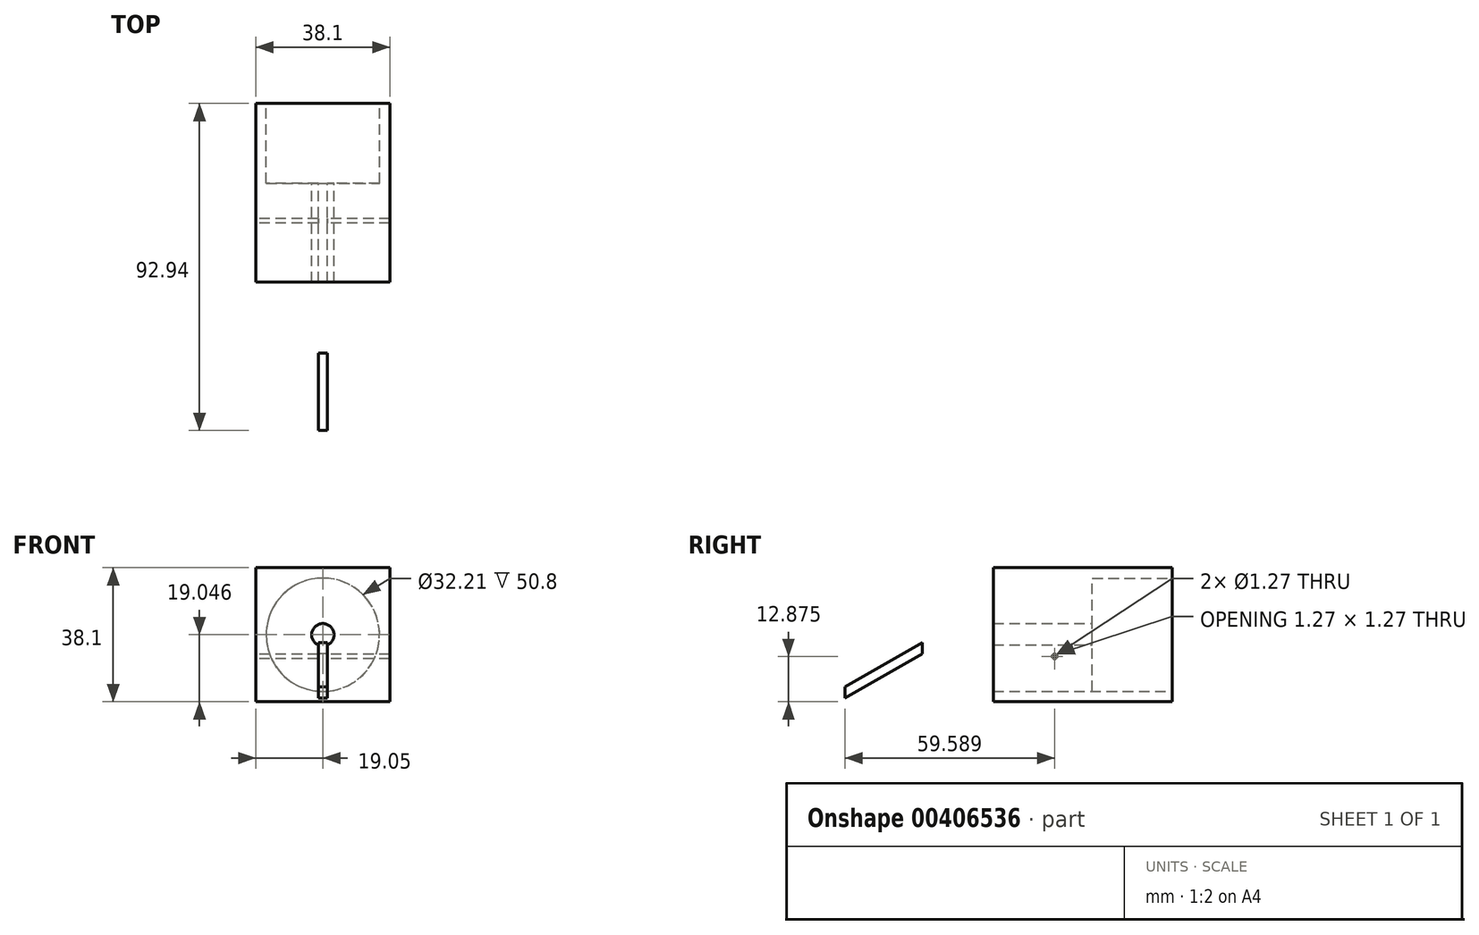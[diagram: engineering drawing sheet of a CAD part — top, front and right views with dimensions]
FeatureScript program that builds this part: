
annotation { "Feature Type Name" : "Feature", "Feature Type Description" : "" }
export const myFeature = defineFeature(function(context is Context, id is Id, definition is map)
    precondition{}
    {
        {
            var Q0;
            Q0=qCreatedBy(makeId("Right.planeOp"),FACE);
            var sketch = newSketch(context, id + "F0", { "sketchPlane" : qUnion([Q0])});
            skLineSegment(sketch, "E0.bottom", {"start": v(-13.06, 8.82) * mm, "end": v(37.74, 8.82) * mm});
            skLineSegment(sketch, "E0.top", {"start": v(-13.06, -29.28) * mm, "end": v(37.74, -29.28) * mm});
            skLineSegment(sketch, "E0.left", {"start": v(-13.06, 8.82) * mm, "end": v(-13.06, -29.28) * mm});
            skLineSegment(sketch, "E0.right", {"start": v(37.74, 8.82) * mm, "end": v(37.74, -29.28) * mm});
            skPoint(sketch, "E1", {"position": v(12.34, -10.23) * mm});
            skPoint(sketch, "E1.positionSnap0", {"position": v(12.34, 8.82) * mm});
            skPoint(sketch, "E1.positionSnap1", {"position": v(37.74, -10.23) * mm});
            skPoint(sketch, "E2", {"position": v(4.28, -10.23) * mm});
            skPoint(sketch, "E3", {"position": v(-3.68, -16.4) * mm});
            skPoint(sketch, "E4", {"position": v(4.28, -13.4) * mm});
            skPoint(sketch, "E5", {"position": v(4.28, -7.06) * mm});
            skLineSegment(sketch, "E6", {"start": v(4.28, -10.23) * mm, "end": v(4.28, -13.4) * mm});
            skPoint(sketch, "E7", {"position": v(-41.1, -18.58) * mm});
            skLineSegment(sketch, "E8", {"start": v(-33.14, -12.41) * mm, "end": v(-33.14, -15.59) * mm});
            skLineSegment(sketch, "E9", {"start": v(-33.14, -15.59) * mm, "end": v(-55.2, -28.18) * mm});
            skLineSegment(sketch, "E10", {"start": v(-33.14, -12.41) * mm, "end": v(-55.15, -25.09) * mm});
            skLineSegment(sketch, "E11", {"start": v(-55.15, -25.09) * mm, "end": v(-55.2, -28.18) * mm});
            skPoint(sketch, "E12", {"position": v(14.98, -10.23) * mm});
            skPoint(sketch, "E13", {"position": v(-33.14, -18.58) * mm});
            skPoint(sketch, "E14", {"position": v(12.34, -16.4) * mm});
            skPoint(sketch, "E15", {"position": v(4.39, -16.4) * mm});
            skCircle(sketch, "E16", {"center": v(4.39, -16.4) * mm, "radius": 0.64 * mm});
            skSolve(sketch);
        }
        {
            var Q0;
            Q0=makeQuery(id+"F0.imprint","IMPRINT",FACE,{"disambiguationData":[TD([[makeQuery(id+"F0.imprint","IMPRINT",EDGE,{"derivedFrom":sQuery(id+"F0.wireOp",EDGE,"E0.bottom")}),-1.0]])]});
            extrude(context, id + "F1", {"entities" : qUnion([Q0]), "endBound" : BoundingType.SYMMETRIC, "depth" : 38.1 * mm, "offsetDistance" : 25.4 * mm});
        }
        {
            var Q0;
            Q0=makeQuery(id+"F1.opExtrude","SWEPT_FACE",FACE,{"disambiguationData":[OSD([sQuery(id+"F0.wireOp",EDGE,"E0.right")])]});
            var sketch = newSketch(context, id + "F2", { "sketchPlane" : qUnion([Q0])});
            skPoint(sketch, "E17", {"position": v(0, -10.23) * mm});
            skPoint(sketch, "E17.positionSnap0", {"position": v(19.05, -10.23) * mm});
            skPoint(sketch, "E17.positionSnap1", {"position": v(0, -29.28) * mm});
            skCircle(sketch, "E18", {"center": v(0, -10.23) * mm, "radius": 16.1 * mm});
            skCircle(sketch, "E19", {"center": v(0, -10.23) * mm, "radius": 3.18 * mm});
            skPoint(sketch, "E20", {"position": v(-1.27, -29.28) * mm});
            skPoint(sketch, "E21.MirrorP", {"position": v(1.27, -29.28) * mm});
            skLineSegment(sketch, "E22", {"start": v(-1.27, -29.28) * mm, "end": v(-1.27, -13.14) * mm});
            skLineSegment(sketch, "E23", {"start": v(1.27, -29.28) * mm, "end": v(1.27, -13.14) * mm});
            skSolve(sketch);
        }
        {
            var Q0;
            Q0=makeQuery(id+"F2.imprint","IMPRINT",FACE,{"disambiguationData":[TD([[makeQuery(id+"F2.imprint","IMPRINT",EDGE,{"derivedFrom":sQuery(id+"F2.wireOp",EDGE,"E18")}),1.0]])]});
            extrude(context, id + "F3", {"entities" : qUnion([Q0]), "operationType" : NewBodyOperationType.REMOVE, "oppositeDirection" : true, "depth" : 22.68 * mm, "offsetDistance" : 25.4 * mm});
        }
        {
            var Q0;
            Q0=makeQuery(id+"F3.boolean.opBoolean","SPLIT",FACE,{"disambiguationData":[TD([makeQuery(id+"F3.opExtrude","SWEPT_FACE",FACE,{"disambiguationData":[OSD([sQuery(id+"F2.wireOp",EDGE,"E19")])]})])],"derivedFrom":makeQuery(id+"F1.opExtrude","SWEPT_FACE",FACE,{"disambiguationData":[OSD([sQuery(id+"F0.wireOp",EDGE,"E0.right")])]})});
            var Q1;
            {var subQ0=sQuery(id+"F2.wireOp",EDGE,"E22");var subQ1=sQuery(id+"F2.wireOp",EDGE,"E18");var subQ2=makeQuery(id+"F2.imprint","INTERSECT",VERTEX,{"derivedFrom":[subQ1,subQ0]});Q1=makeQuery(id+"F2.imprint","IMPRINT",FACE,{"disambiguationData":[TD([[makeQuery(id+"F2.imprint","IMPRINT",EDGE,{"disambiguationData":[TD([[subQ2,-1.0]])],"derivedFrom":subQ1}),1.0]])]});}
            extrude(context, id + "F4", {"entities" : qUnion([Q0, Q1]), "operationType" : NewBodyOperationType.REMOVE, "endBound" : BoundingType.THROUGH_ALL, "oppositeDirection" : true, "depth" : 25.4 * mm, "offsetDistance" : 25.4 * mm});
        }
        {
            var Q0;
            Q0=makeQuery(id+"F0.imprint","IMPRINT",FACE,{"disambiguationData":[TD([[makeQuery(id+"F0.imprint","IMPRINT",EDGE,{"derivedFrom":sQuery(id+"F0.wireOp",EDGE,"E8")}),-1.0]])]});
            extrude(context, id + "F5", {"entities" : qUnion([Q0]), "endBound" : BoundingType.SYMMETRIC, "depth" : 2.54 * mm, "offsetDistance" : 25.4 * mm});
        }
    });
